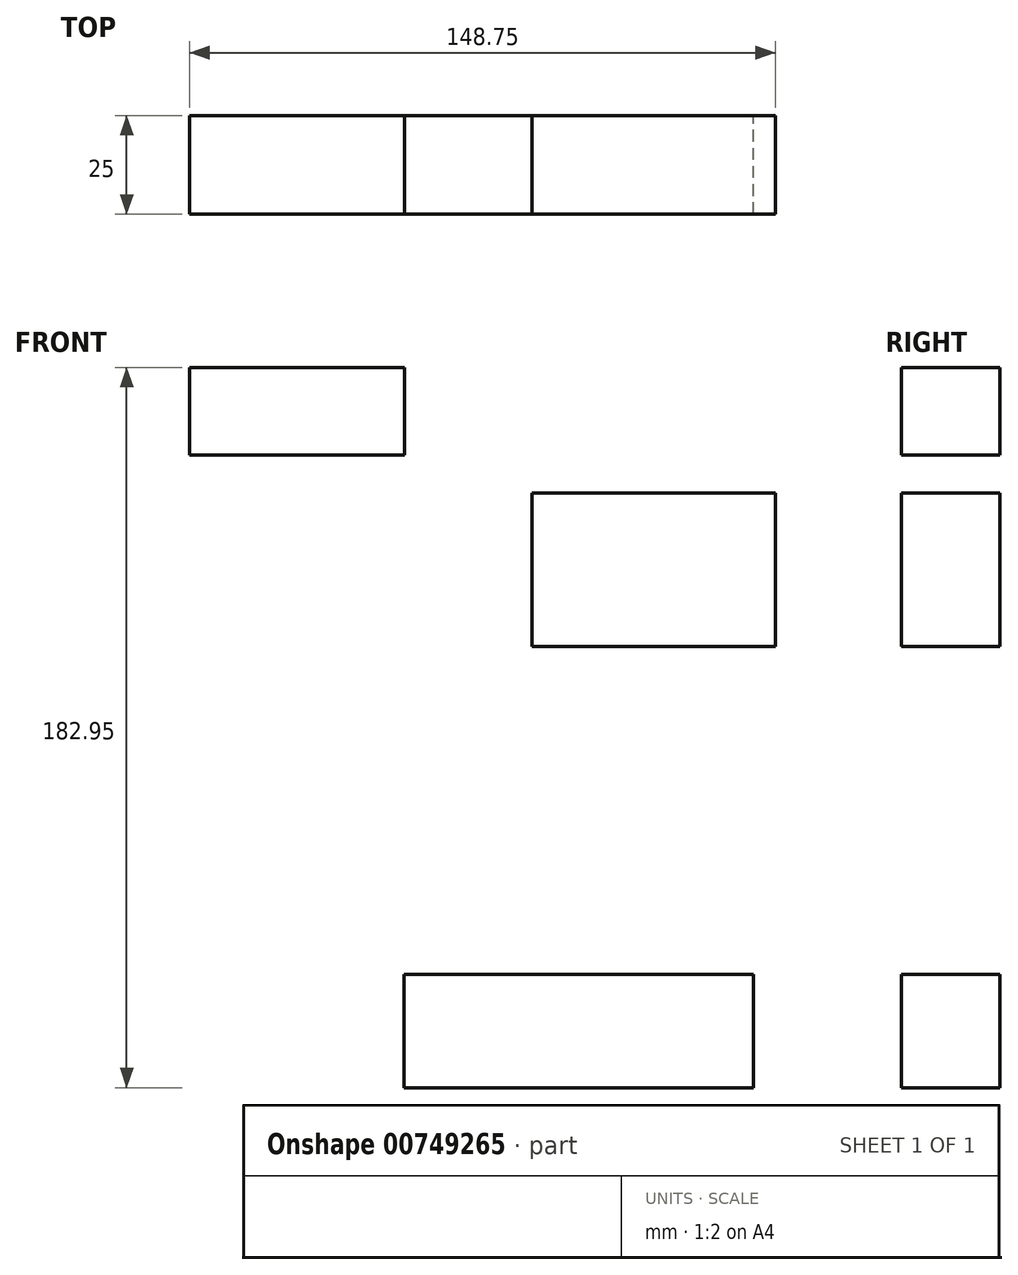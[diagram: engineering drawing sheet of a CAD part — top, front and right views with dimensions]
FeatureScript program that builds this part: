
annotation { "Feature Type Name" : "Feature", "Feature Type Description" : "" }
export const myFeature = defineFeature(function(context is Context, id is Id, definition is map)
    precondition{}
    {
        {
            var Q0;
            Q0=qCreatedBy(makeId("Front.planeOp"),FACE);
            var sketch = newSketch(context, id + "F0", { "sketchPlane" : qUnion([Q0])});
            skLineSegment(sketch, "E0.bottom", {"start": v(-54.58, 121.22) * mm, "end": v(0, 121.22) * mm});
            skLineSegment(sketch, "E0.top", {"start": v(-54.58, 99.03) * mm, "end": v(0, 99.03) * mm});
            skLineSegment(sketch, "E0.left", {"start": v(-54.58, 121.22) * mm, "end": v(-54.58, 99.03) * mm});
            skLineSegment(sketch, "E0.right", {"start": v(0, 121.22) * mm, "end": v(0, 99.03) * mm});
            skLineSegment(sketch, "E1.bottom", {"start": v(32.3, 89.3) * mm, "end": v(94.17, 89.3) * mm});
            skLineSegment(sketch, "E1.top", {"start": v(32.3, 50.4) * mm, "end": v(94.17, 50.4) * mm});
            skLineSegment(sketch, "E1.left", {"start": v(32.3, 89.3) * mm, "end": v(32.3, 50.4) * mm});
            skLineSegment(sketch, "E1.right", {"start": v(94.17, 89.3) * mm, "end": v(94.17, 50.4) * mm});
            skLineSegment(sketch, "E2.bottom", {"start": v(-0.14, -32.9) * mm, "end": v(88.6, -32.9) * mm});
            skLineSegment(sketch, "E2.top", {"start": v(-0.14, -61.73) * mm, "end": v(88.6, -61.73) * mm});
            skLineSegment(sketch, "E2.left", {"start": v(-0.14, -32.9) * mm, "end": v(-0.14, -61.73) * mm});
            skLineSegment(sketch, "E2.right", {"start": v(88.6, -32.9) * mm, "end": v(88.6, -61.73) * mm});
            skSolve(sketch);
        }
        {
            var Q0;
            Q0 = qSketchRegion(id + "F0", true);
            extrude(context, id + "F1", {"entities" : qUnion([Q0]), "depth" : 25 * mm, "offsetDistance" : 25 * mm});
        }
    });
